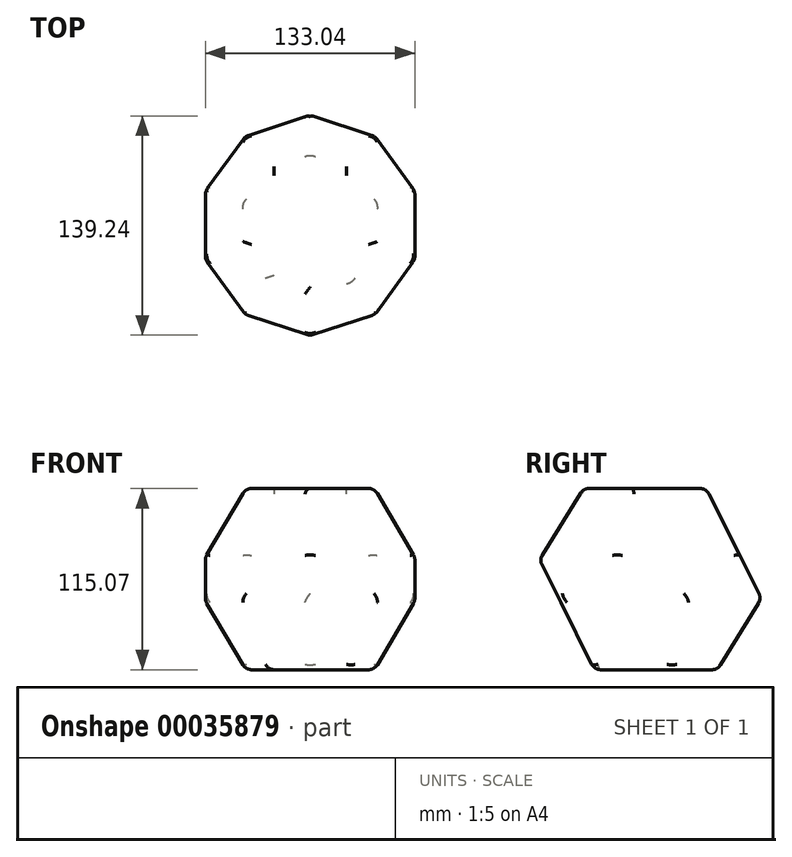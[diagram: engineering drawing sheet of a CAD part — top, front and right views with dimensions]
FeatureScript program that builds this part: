
annotation { "Feature Type Name" : "Feature", "Feature Type Description" : "" }
export const myFeature = defineFeature(function(context is Context, id is Id, definition is map)
    precondition{}
    {
        {
            var Q0;
            Q0=qCreatedBy(makeId("Right.planeOp"),FACE);
            var sketch = newSketch(context, id + "F0", { "sketchPlane" : qUnion([Q0])});
            skLineSegment(sketch, "E0.0", {"start": v(0, 133) * mm, "end": v(-82.2, 0) * mm});
            skPoint(sketch, "E1.orphan", {"position": v(-50.8, 50.8) * mm});
            skPoint(sketch, "E2.orphan", {"position": v(-31.4, 82.2) * mm});
            skLineSegment(sketch, "E3", {"start": v(0, 82.2) * mm, "end": v(0, 0) * mm});
            skLineSegment(sketch, "E4", {"start": v(0, 41.1) * mm, "end": v(84.2, 41.1) * mm});
            skSolve(sketch);
        }
        {
            var Q0;
            Q0=qCreatedBy(makeId("Top.planeOp"),FACE);
            var sketch = newSketch(context, id + "F1", { "sketchPlane" : qUnion([Q0])});
            skCircle(sketch, "E5.cCircle", {"center": v(0, 0) * mm, "radius": 66.5 * mm, "construction": true});
            skLineSegment(sketch, "E5.0", {"start": v(78.17, -25.4) * mm, "end": v(0, -82.2) * mm});
            skLineSegment(sketch, "E5.1", {"start": v(0, -82.2) * mm, "end": v(-78.17, -25.4) * mm});
            skLineSegment(sketch, "E5.2", {"start": v(-78.17, -25.4) * mm, "end": v(-48.31, 66.5) * mm});
            skLineSegment(sketch, "E5.3", {"start": v(-48.31, 66.5) * mm, "end": v(48.31, 66.5) * mm});
            skLineSegment(sketch, "E5.4", {"start": v(48.31, 66.5) * mm, "end": v(78.17, -25.4) * mm});
            skPoint(sketch, "E5.0.midPoint", {"position": v(39.09, -53.8) * mm});
            skSolve(sketch);
        }
        {
            var Q1;
            Q1=qSketchRegion(id+"F1",true);
            var Q2;
            Q2=sQuery(id+"F0.wireOp",VERTEX,"E0.0.start");
            loft(context, id + "F2", {"sheetProfilesArray" : [{ "sheetProfileEntities" : qUnion([Q1]) }, { "sheetProfileEntities" : qUnion([Q2]) }]});
        }
        {
            var Q0;
            Q0=makeQuery(id+"F2.opLoft","SWEPT_BODY",BODY,{"disambiguationData":[OSD([makeQuery(id+"F1.imprint","IMPRINT",FACE,{"disambiguationData":[TD([[makeQuery(id+"F1.imprint","IMPRINT",EDGE,{"derivedFrom":sQuery(id+"F1.wireOp",EDGE,"E5.0")}),-1.0]])]})])]});
            var Q1;
            Q1=sQuery(id+"F0.wireOp",EDGE,"E4");
            transform(context, id + "F3", {"entities" : qUnion([Q0]), "transformType" : TransformType.ROTATION, "transformAxis" : qUnion([Q1]), "angle" : 180 * degree, "makeCopy" : true});
        }
        {
            var Q0;
            Q0=makeQuery(id+"F3.opPattern","COPY",BODY,{"derivedFrom":makeQuery(id+"F2.opLoft","SWEPT_BODY",BODY,{"disambiguationData":[OSD([makeQuery(id+"F1.imprint","IMPRINT",FACE,{"disambiguationData":[TD([[makeQuery(id+"F1.imprint","IMPRINT",EDGE,{"derivedFrom":sQuery(id+"F1.wireOp",EDGE,"E5.0")}),-1.0]])]})])]}),"instanceName":"1"});
            var Q1;
            Q1=sQuery(id+"F0.wireOp",EDGE,"E3");
            transform(context, id + "F4", {"entities" : qUnion([Q0]), "transformType" : TransformType.ROTATION, "transformAxis" : qUnion([Q1]), "angle" : 36 * degree, "makeCopy" : false});
        }
        {
            var Q0;
            Q0=makeQuery(id+"F2.opLoft","SWEPT_BODY",BODY,{"disambiguationData":[OSD([makeQuery(id+"F1.imprint","IMPRINT",FACE,{"disambiguationData":[TD([[makeQuery(id+"F1.imprint","IMPRINT",EDGE,{"derivedFrom":sQuery(id+"F1.wireOp",EDGE,"E5.0")}),-1.0]])]})])]});
            var Q1;
            Q1=makeQuery(id+"F3.opPattern","COPY",BODY,{"derivedFrom":makeQuery(id+"F2.opLoft","SWEPT_BODY",BODY,{"disambiguationData":[OSD([makeQuery(id+"F1.imprint","IMPRINT",FACE,{"disambiguationData":[TD([[makeQuery(id+"F1.imprint","IMPRINT",EDGE,{"derivedFrom":sQuery(id+"F1.wireOp",EDGE,"E5.0")}),-1.0]])]})])]}),"instanceName":"1"});
            booleanBodies(context, id + "F5", {"operationType" : BooleanOperationType.INTERSECTION, "tools" : qUnion([Q0, Q1])});
        }
        {
            var Q0;
            {var subQ0=makeQuery(id+"F2.opLoft","SWEPT_BODY",BODY,{"disambiguationData":[OSD([sQuery(id+"F0.wireOp",VERTEX,"E0.0.start"),makeQuery(id+"F1.imprint","IMPRINT",FACE,{"disambiguationData":[TD([[makeQuery(id+"F1.imprint","IMPRINT",EDGE,{"derivedFrom":sQuery(id+"F1.wireOp",EDGE,"E5.0")}),-1.0]])]})])]});Q0=makeQuery(id+"F5.opBoolean","INTERSECT",BODY,{"derivedFrom":[subQ0,makeQuery(id+"F3.opPattern","COPY",BODY,{"derivedFrom":subQ0,"instanceName":"1"})]});}
            var Q1;
            Q1=qCreatedBy(makeId("Origin.pointOp"),VERTEX);
            transform(context, id + "F6", {"entities" : qUnion([Q0]), "transformType" : TransformType.SCALE_UNIFORMLY, "scale" : 1.4, "makeCopy" : false, "scalePoint" : qUnion([Q1])});
        }
        {
            var Q0;
            {var subQ0=sQuery(id+"F1.wireOp",EDGE,"E5.3");Q0=makeQuery(id+"F5.opBoolean","INTERSECT",EDGE,{"derivedFrom":[makeQuery(id+"F2.opLoft","SWEPT_FACE",FACE,{"disambiguationData":[OSD([sQuery(id+"F1.wireOp",EDGE,"E5.0"),subQ0,sQuery(id+"F1.wireOp",EDGE,"E5.4")])]}),makeQuery(id+"F3.opPattern","COPY",FACE,{"derivedFrom":makeQuery(id+"F2.opLoft","SWEPT_FACE",FACE,{"disambiguationData":[OSD([sQuery(id+"F1.wireOp",EDGE,"E5.1"),sQuery(id+"F1.wireOp",EDGE,"E5.2"),subQ0])]}),"instanceName":"1"})]});}
            var Q1;
            Q1=makeQuery(id+"F2.opLoft","SWEPT_EDGE",EDGE,{"disambiguationData":[OSD([sQuery(id+"F0.wireOp",VERTEX,"E0.0.start"),sQuery(id+"F1.wireOp",EDGE,"E5.0"),sQuery(id+"F1.wireOp",EDGE,"E5.4")])]});
            var Q2;
            {var subQ0=sQuery(id+"F1.wireOp",EDGE,"E5.0");var subQ1=sQuery(id+"F1.wireOp",EDGE,"E5.1");Q2=makeQuery(id+"F5.opBoolean","INTERSECT",EDGE,{"derivedFrom":[makeQuery(id+"F2.opLoft","SWEPT_FACE",FACE,{"disambiguationData":[OSD([subQ0,subQ1,sQuery(id+"F1.wireOp",EDGE,"E5.2")])]}),makeQuery(id+"F3.opPattern","COPY",FACE,{"derivedFrom":makeQuery(id+"F2.opLoft","SWEPT_FACE",FACE,{"disambiguationData":[OSD([subQ0,subQ1,sQuery(id+"F1.wireOp",EDGE,"E5.4")])]}),"instanceName":"1"})]});}
            var Q3;
            Q3=makeQuery(id+"F2.opLoft","SWEPT_EDGE",EDGE,{"disambiguationData":[OSD([sQuery(id+"F0.wireOp",VERTEX,"E0.0.start"),sQuery(id+"F1.wireOp",EDGE,"E5.1"),sQuery(id+"F1.wireOp",EDGE,"E5.2")])]});
            var Q4;
            {var subQ0=sQuery(id+"F1.wireOp",EDGE,"E5.2");var subQ1=sQuery(id+"F1.wireOp",EDGE,"E5.1");var subQ2=sQuery(id+"F1.wireOp",EDGE,"E5.0");Q4=makeQuery(id+"F5.opBoolean","INTERSECT",EDGE,{"derivedFrom":[makeQuery(id+"F2.opLoft","CAP_FACE",FACE,{"disambiguationData":[OSD([makeQuery(id+"F1.imprint","IMPRINT",FACE,{"disambiguationData":[TD([[makeQuery(id+"F1.imprint","IMPRINT",EDGE,{"derivedFrom":subQ2}),-1.0]])]})])],"isStart":true}),makeQuery(id+"F3.opPattern","COPY",FACE,{"derivedFrom":makeQuery(id+"F2.opLoft","SWEPT_FACE",FACE,{"disambiguationData":[OSD([subQ2,subQ1,subQ0])]}),"instanceName":"1"})]});}
            var Q5;
            Q5=makeQuery(id+"F3.opPattern","COPY",EDGE,{"derivedFrom":makeQuery(id+"F2.opLoft","SWEPT_EDGE",EDGE,{"disambiguationData":[OSD([sQuery(id+"F0.wireOp",VERTEX,"E0.0.start"),sQuery(id+"F1.wireOp",EDGE,"E5.0"),sQuery(id+"F1.wireOp",EDGE,"E5.4")])]}),"instanceName":"1"});
            var Q6;
            Q6=makeQuery(id+"F3.opPattern","COPY",EDGE,{"derivedFrom":makeQuery(id+"F2.opLoft","SWEPT_EDGE",EDGE,{"disambiguationData":[OSD([sQuery(id+"F0.wireOp",VERTEX,"E0.0.start"),sQuery(id+"F1.wireOp",EDGE,"E5.0"),sQuery(id+"F1.wireOp",EDGE,"E5.1")])]}),"instanceName":"1"});
            var Q7;
            Q7=makeQuery(id+"F3.opPattern","COPY",EDGE,{"derivedFrom":makeQuery(id+"F2.opLoft","SWEPT_EDGE",EDGE,{"disambiguationData":[OSD([sQuery(id+"F0.wireOp",VERTEX,"E0.0.start"),sQuery(id+"F1.wireOp",EDGE,"E5.2"),sQuery(id+"F1.wireOp",EDGE,"E5.3")])]}),"instanceName":"1"});
            var Q8;
            {var subQ0=sQuery(id+"F1.wireOp",EDGE,"E5.0");var subQ1=sQuery(id+"F1.wireOp",EDGE,"E5.1");Q8=makeQuery(id+"F5.opBoolean","INTERSECT",EDGE,{"derivedFrom":[makeQuery(id+"F2.opLoft","SWEPT_FACE",FACE,{"disambiguationData":[OSD([subQ0,subQ1,sQuery(id+"F1.wireOp",EDGE,"E5.4")])]}),makeQuery(id+"F3.opPattern","COPY",FACE,{"derivedFrom":makeQuery(id+"F2.opLoft","SWEPT_FACE",FACE,{"disambiguationData":[OSD([subQ0,subQ1,sQuery(id+"F1.wireOp",EDGE,"E5.2")])]}),"instanceName":"1"})]});}
            var Q9;
            {var subQ0=sQuery(id+"F1.wireOp",EDGE,"E5.4");var subQ1=sQuery(id+"F1.wireOp",EDGE,"E5.3");var subQ2=sQuery(id+"F1.wireOp",EDGE,"E5.2");Q9=makeQuery(id+"F5.opBoolean","INTERSECT",EDGE,{"derivedFrom":[makeQuery(id+"F2.opLoft","CAP_FACE",FACE,{"disambiguationData":[OSD([makeQuery(id+"F1.imprint","IMPRINT",FACE,{"disambiguationData":[TD([[makeQuery(id+"F1.imprint","IMPRINT",EDGE,{"derivedFrom":sQuery(id+"F1.wireOp",EDGE,"E5.0")}),-1.0]])]})])],"isStart":true}),makeQuery(id+"F3.opPattern","COPY",FACE,{"derivedFrom":makeQuery(id+"F2.opLoft","SWEPT_FACE",FACE,{"disambiguationData":[OSD([subQ2,subQ1,subQ0])]}),"instanceName":"1"})]});}
            var Q10;
            {var subQ0=sQuery(id+"F1.wireOp",EDGE,"E5.1");Q10=makeQuery(id+"F5.opBoolean","INTERSECT",EDGE,{"derivedFrom":[makeQuery(id+"F2.opLoft","SWEPT_FACE",FACE,{"disambiguationData":[OSD([sQuery(id+"F1.wireOp",EDGE,"E5.0"),subQ0,sQuery(id+"F1.wireOp",EDGE,"E5.4")])]}),makeQuery(id+"F3.opPattern","COPY",FACE,{"derivedFrom":makeQuery(id+"F2.opLoft","SWEPT_FACE",FACE,{"disambiguationData":[OSD([subQ0,sQuery(id+"F1.wireOp",EDGE,"E5.2"),sQuery(id+"F1.wireOp",EDGE,"E5.3")])]}),"instanceName":"1"})]});}
            var Q11;
            {var subQ0=sQuery(id+"F1.wireOp",EDGE,"E5.0");var subQ1=sQuery(id+"F1.wireOp",EDGE,"E5.1");var subQ2=sQuery(id+"F1.wireOp",EDGE,"E5.2");Q11=makeQuery(id+"F5.opBoolean","INTERSECT",EDGE,{"derivedFrom":[makeQuery(id+"F2.opLoft","SWEPT_FACE",FACE,{"disambiguationData":[OSD([subQ0,subQ1,subQ2])]}),makeQuery(id+"F3.opPattern","COPY",FACE,{"derivedFrom":makeQuery(id+"F2.opLoft","CAP_FACE",FACE,{"disambiguationData":[OSD([makeQuery(id+"F1.imprint","IMPRINT",FACE,{"disambiguationData":[TD([[makeQuery(id+"F1.imprint","IMPRINT",EDGE,{"derivedFrom":subQ0}),-1.0]])]})])],"isStart":true}),"instanceName":"1"})]});}
            var Q12;
            {var subQ0=sQuery(id+"F1.wireOp",EDGE,"E5.3");var subQ1=sQuery(id+"F1.wireOp",EDGE,"E5.2");var subQ2=sQuery(id+"F1.wireOp",EDGE,"E5.1");Q12=makeQuery(id+"F5.opBoolean","INTERSECT",EDGE,{"derivedFrom":[makeQuery(id+"F2.opLoft","CAP_FACE",FACE,{"disambiguationData":[OSD([makeQuery(id+"F1.imprint","IMPRINT",FACE,{"disambiguationData":[TD([[makeQuery(id+"F1.imprint","IMPRINT",EDGE,{"derivedFrom":sQuery(id+"F1.wireOp",EDGE,"E5.0")}),-1.0]])]})])],"isStart":true}),makeQuery(id+"F3.opPattern","COPY",FACE,{"derivedFrom":makeQuery(id+"F2.opLoft","SWEPT_FACE",FACE,{"disambiguationData":[OSD([subQ2,subQ1,subQ0])]}),"instanceName":"1"})]});}
            var Q13;
            {var subQ0=sQuery(id+"F1.wireOp",EDGE,"E5.4");var subQ1=sQuery(id+"F1.wireOp",EDGE,"E5.3");var subQ2=sQuery(id+"F1.wireOp",EDGE,"E5.0");Q13=makeQuery(id+"F5.opBoolean","INTERSECT",EDGE,{"derivedFrom":[makeQuery(id+"F2.opLoft","CAP_FACE",FACE,{"disambiguationData":[OSD([makeQuery(id+"F1.imprint","IMPRINT",FACE,{"disambiguationData":[TD([[makeQuery(id+"F1.imprint","IMPRINT",EDGE,{"derivedFrom":subQ2}),-1.0]])]})])],"isStart":true}),makeQuery(id+"F3.opPattern","COPY",FACE,{"derivedFrom":makeQuery(id+"F2.opLoft","SWEPT_FACE",FACE,{"disambiguationData":[OSD([subQ2,subQ1,subQ0])]}),"instanceName":"1"})]});}
            var Q14;
            {var subQ0=sQuery(id+"F1.wireOp",EDGE,"E5.1");Q14=makeQuery(id+"F5.opBoolean","INTERSECT",EDGE,{"derivedFrom":[makeQuery(id+"F2.opLoft","SWEPT_FACE",FACE,{"disambiguationData":[OSD([subQ0,sQuery(id+"F1.wireOp",EDGE,"E5.2"),sQuery(id+"F1.wireOp",EDGE,"E5.3")])]}),makeQuery(id+"F3.opPattern","COPY",FACE,{"derivedFrom":makeQuery(id+"F2.opLoft","SWEPT_FACE",FACE,{"disambiguationData":[OSD([sQuery(id+"F1.wireOp",EDGE,"E5.0"),subQ0,sQuery(id+"F1.wireOp",EDGE,"E5.4")])]}),"instanceName":"1"})]});}
            var Q15;
            {var subQ0=makeQuery(id+"F2.opLoft","SWEPT_FACE",FACE,{"disambiguationData":[OSD([sQuery(id+"F1.wireOp",EDGE,"E5.0"),sQuery(id+"F1.wireOp",EDGE,"E5.1"),sQuery(id+"F1.wireOp",EDGE,"E5.2")])]});Q15=makeQuery(id+"F5.opBoolean","INTERSECT",EDGE,{"derivedFrom":[subQ0,makeQuery(id+"F3.opPattern","COPY",FACE,{"derivedFrom":subQ0,"instanceName":"1"})]});}
            var Q16;
            {var subQ0=sQuery(id+"F1.wireOp",EDGE,"E5.3");var subQ1=sQuery(id+"F1.wireOp",EDGE,"E5.4");Q16=makeQuery(id+"F5.opBoolean","INTERSECT",EDGE,{"derivedFrom":[makeQuery(id+"F2.opLoft","SWEPT_FACE",FACE,{"disambiguationData":[OSD([sQuery(id+"F1.wireOp",EDGE,"E5.0"),subQ0,subQ1])]}),makeQuery(id+"F3.opPattern","COPY",FACE,{"derivedFrom":makeQuery(id+"F2.opLoft","SWEPT_FACE",FACE,{"disambiguationData":[OSD([sQuery(id+"F1.wireOp",EDGE,"E5.2"),subQ0,subQ1])]}),"instanceName":"1"})]});}
            var Q17;
            {var subQ0=sQuery(id+"F1.wireOp",EDGE,"E5.0");var subQ1=sQuery(id+"F1.wireOp",EDGE,"E5.3");var subQ2=sQuery(id+"F1.wireOp",EDGE,"E5.4");Q17=makeQuery(id+"F5.opBoolean","INTERSECT",EDGE,{"derivedFrom":[makeQuery(id+"F2.opLoft","SWEPT_FACE",FACE,{"disambiguationData":[OSD([subQ0,subQ1,subQ2])]}),makeQuery(id+"F3.opPattern","COPY",FACE,{"derivedFrom":makeQuery(id+"F2.opLoft","CAP_FACE",FACE,{"disambiguationData":[OSD([makeQuery(id+"F1.imprint","IMPRINT",FACE,{"disambiguationData":[TD([[makeQuery(id+"F1.imprint","IMPRINT",EDGE,{"derivedFrom":subQ0}),-1.0]])]})])],"isStart":true}),"instanceName":"1"})]});}
            var Q18;
            Q18=makeQuery(id+"F2.opLoft","SWEPT_EDGE",EDGE,{"disambiguationData":[OSD([sQuery(id+"F0.wireOp",VERTEX,"E0.0.start"),sQuery(id+"F1.wireOp",EDGE,"E5.0"),sQuery(id+"F1.wireOp",EDGE,"E5.1")])]});
            var Q19;
            Q19=makeQuery(id+"F2.opLoft","SWEPT_EDGE",EDGE,{"disambiguationData":[OSD([sQuery(id+"F0.wireOp",VERTEX,"E0.0.start"),sQuery(id+"F1.wireOp",EDGE,"E5.2"),sQuery(id+"F1.wireOp",EDGE,"E5.3")])]});
            var Q20;
            Q20=makeQuery(id+"F2.opLoft","SWEPT_EDGE",EDGE,{"disambiguationData":[OSD([sQuery(id+"F0.wireOp",VERTEX,"E0.0.start"),sQuery(id+"F1.wireOp",EDGE,"E5.3"),sQuery(id+"F1.wireOp",EDGE,"E5.4")])]});
            var Q21;
            {var subQ0=sQuery(id+"F1.wireOp",EDGE,"E5.4");var subQ1=sQuery(id+"F1.wireOp",EDGE,"E5.1");var subQ2=sQuery(id+"F1.wireOp",EDGE,"E5.0");Q21=makeQuery(id+"F5.opBoolean","INTERSECT",EDGE,{"derivedFrom":[makeQuery(id+"F2.opLoft","CAP_FACE",FACE,{"disambiguationData":[OSD([makeQuery(id+"F1.imprint","IMPRINT",FACE,{"disambiguationData":[TD([[makeQuery(id+"F1.imprint","IMPRINT",EDGE,{"derivedFrom":subQ2}),-1.0]])]})])],"isStart":true}),makeQuery(id+"F3.opPattern","COPY",FACE,{"derivedFrom":makeQuery(id+"F2.opLoft","SWEPT_FACE",FACE,{"disambiguationData":[OSD([subQ2,subQ1,subQ0])]}),"instanceName":"1"})]});}
            var Q22;
            {var subQ0=makeQuery(id+"F2.opLoft","SWEPT_FACE",FACE,{"disambiguationData":[OSD([sQuery(id+"F1.wireOp",EDGE,"E5.2"),sQuery(id+"F1.wireOp",EDGE,"E5.3"),sQuery(id+"F1.wireOp",EDGE,"E5.4")])]});Q22=makeQuery(id+"F5.opBoolean","INTERSECT",EDGE,{"derivedFrom":[subQ0,makeQuery(id+"F3.opPattern","COPY",FACE,{"derivedFrom":subQ0,"instanceName":"1"})]});}
            var Q23;
            Q23=makeQuery(id+"F3.opPattern","COPY",EDGE,{"derivedFrom":makeQuery(id+"F2.opLoft","SWEPT_EDGE",EDGE,{"disambiguationData":[OSD([sQuery(id+"F0.wireOp",VERTEX,"E0.0.start"),sQuery(id+"F1.wireOp",EDGE,"E5.1"),sQuery(id+"F1.wireOp",EDGE,"E5.2")])]}),"instanceName":"1"});
            var Q24;
            {var subQ0=sQuery(id+"F1.wireOp",EDGE,"E5.3");var subQ1=sQuery(id+"F1.wireOp",EDGE,"E5.4");Q24=makeQuery(id+"F5.opBoolean","INTERSECT",EDGE,{"derivedFrom":[makeQuery(id+"F2.opLoft","SWEPT_FACE",FACE,{"disambiguationData":[OSD([sQuery(id+"F1.wireOp",EDGE,"E5.2"),subQ0,subQ1])]}),makeQuery(id+"F3.opPattern","COPY",FACE,{"derivedFrom":makeQuery(id+"F2.opLoft","SWEPT_FACE",FACE,{"disambiguationData":[OSD([sQuery(id+"F1.wireOp",EDGE,"E5.0"),subQ0,subQ1])]}),"instanceName":"1"})]});}
            var Q25;
            Q25=makeQuery(id+"F3.opPattern","COPY",EDGE,{"derivedFrom":makeQuery(id+"F2.opLoft","SWEPT_EDGE",EDGE,{"disambiguationData":[OSD([sQuery(id+"F0.wireOp",VERTEX,"E0.0.start"),sQuery(id+"F1.wireOp",EDGE,"E5.3"),sQuery(id+"F1.wireOp",EDGE,"E5.4")])]}),"instanceName":"1"});
            var Q26;
            {var subQ0=sQuery(id+"F1.wireOp",EDGE,"E5.3");Q26=makeQuery(id+"F5.opBoolean","INTERSECT",EDGE,{"derivedFrom":[makeQuery(id+"F2.opLoft","SWEPT_FACE",FACE,{"disambiguationData":[OSD([sQuery(id+"F1.wireOp",EDGE,"E5.1"),sQuery(id+"F1.wireOp",EDGE,"E5.2"),subQ0])]}),makeQuery(id+"F3.opPattern","COPY",FACE,{"derivedFrom":makeQuery(id+"F2.opLoft","SWEPT_FACE",FACE,{"disambiguationData":[OSD([sQuery(id+"F1.wireOp",EDGE,"E5.0"),subQ0,sQuery(id+"F1.wireOp",EDGE,"E5.4")])]}),"instanceName":"1"})]});}
            var Q27;
            {var subQ0=sQuery(id+"F1.wireOp",EDGE,"E5.0");var subQ1=sQuery(id+"F1.wireOp",EDGE,"E5.1");var subQ2=sQuery(id+"F1.wireOp",EDGE,"E5.4");Q27=makeQuery(id+"F5.opBoolean","INTERSECT",EDGE,{"derivedFrom":[makeQuery(id+"F2.opLoft","SWEPT_FACE",FACE,{"disambiguationData":[OSD([subQ0,subQ1,subQ2])]}),makeQuery(id+"F3.opPattern","COPY",FACE,{"derivedFrom":makeQuery(id+"F2.opLoft","CAP_FACE",FACE,{"disambiguationData":[OSD([makeQuery(id+"F1.imprint","IMPRINT",FACE,{"disambiguationData":[TD([[makeQuery(id+"F1.imprint","IMPRINT",EDGE,{"derivedFrom":subQ0}),-1.0]])]})])],"isStart":true}),"instanceName":"1"})]});}
            var Q28;
            {var subQ0=sQuery(id+"F1.wireOp",EDGE,"E5.1");var subQ1=sQuery(id+"F1.wireOp",EDGE,"E5.2");var subQ2=sQuery(id+"F1.wireOp",EDGE,"E5.3");Q28=makeQuery(id+"F5.opBoolean","INTERSECT",EDGE,{"derivedFrom":[makeQuery(id+"F2.opLoft","SWEPT_FACE",FACE,{"disambiguationData":[OSD([subQ0,subQ1,subQ2])]}),makeQuery(id+"F3.opPattern","COPY",FACE,{"derivedFrom":makeQuery(id+"F2.opLoft","CAP_FACE",FACE,{"disambiguationData":[OSD([makeQuery(id+"F1.imprint","IMPRINT",FACE,{"disambiguationData":[TD([[makeQuery(id+"F1.imprint","IMPRINT",EDGE,{"derivedFrom":sQuery(id+"F1.wireOp",EDGE,"E5.0")}),-1.0]])]})])],"isStart":true}),"instanceName":"1"})]});}
            var Q29;
            {var subQ0=sQuery(id+"F1.wireOp",EDGE,"E5.2");var subQ1=sQuery(id+"F1.wireOp",EDGE,"E5.3");var subQ2=sQuery(id+"F1.wireOp",EDGE,"E5.4");Q29=makeQuery(id+"F5.opBoolean","INTERSECT",EDGE,{"derivedFrom":[makeQuery(id+"F2.opLoft","SWEPT_FACE",FACE,{"disambiguationData":[OSD([subQ0,subQ1,subQ2])]}),makeQuery(id+"F3.opPattern","COPY",FACE,{"derivedFrom":makeQuery(id+"F2.opLoft","CAP_FACE",FACE,{"disambiguationData":[OSD([makeQuery(id+"F1.imprint","IMPRINT",FACE,{"disambiguationData":[TD([[makeQuery(id+"F1.imprint","IMPRINT",EDGE,{"derivedFrom":sQuery(id+"F1.wireOp",EDGE,"E5.0")}),-1.0]])]})])],"isStart":true}),"instanceName":"1"})]});}
            fillet(context, id + "F7", {"entities" : qUnion([Q0, Q1, Q2, Q3, Q4, Q5, Q6, Q7, Q8, Q9, Q10, Q11, Q12, Q13, Q14, Q15, Q16, Q17, Q18, Q19, Q20, Q21, Q22, Q23, Q24, Q25, Q26, Q27, Q28, Q29]), "radius" : 6.35 * mm, "tangentPropagation" : true, "allowEdgeOverflow" : false});
        }
    });
